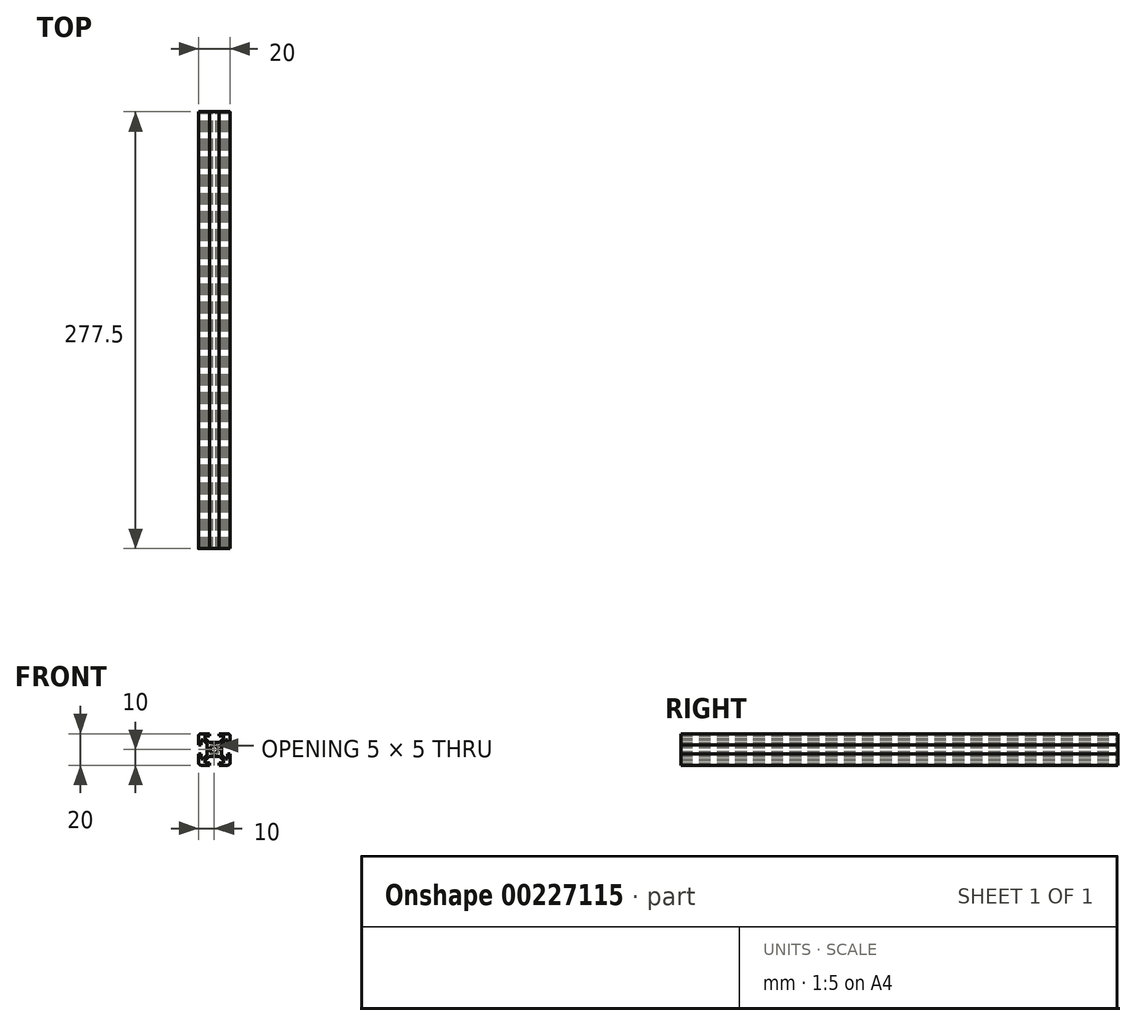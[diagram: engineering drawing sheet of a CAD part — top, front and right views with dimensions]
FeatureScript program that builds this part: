
annotation { "Feature Type Name" : "Feature", "Feature Type Description" : "" }
export const myFeature = defineFeature(function(context is Context, id is Id, definition is map)
    precondition{}
    {
        {
            var Q0;
            Q0=qCreatedBy(makeId("Front.planeOp"),FACE);
            var sketch = newSketch(context, id + "F0", { "sketchPlane" : qUnion([Q0])});
            skLineSegment(sketch, "E0.bottom", {"start": v(8.5, -10) * mm, "end": v(3, -10) * mm});
            skLineSegment(sketch, "E0.top", {"start": v(8.5, 10) * mm, "end": v(3, 10) * mm});
            skLineSegment(sketch, "E0.left", {"start": v(10, -8.5) * mm, "end": v(10, -3) * mm});
            skLineSegment(sketch, "E0.right", {"start": v(-10, -8.5) * mm, "end": v(-10, -3) * mm});
            skPoint(sketch, "E0.middle", {"position": v(0, 0) * mm});
            skLineSegment(sketch, "E1.bottom", {"start": v(6, -8.5) * mm, "end": v(3, -8.5) * mm});
            skLineSegment(sketch, "E1.top", {"start": v(6, 8.5) * mm, "end": v(3, 8.5) * mm});
            skLineSegment(sketch, "E1.left", {"start": v(8.5, -6) * mm, "end": v(8.5, -3) * mm});
            skLineSegment(sketch, "E1.right", {"start": v(-8.5, -6) * mm, "end": v(-8.5, -3) * mm});
            skLineSegment(sketch, "E2.bottom", {"start": v(3.44, -4.5) * mm, "end": v(-3.44, -4.5) * mm});
            skLineSegment(sketch, "E2.top", {"start": v(3.44, 4.5) * mm, "end": v(-3.44, 4.5) * mm});
            skLineSegment(sketch, "E2.left", {"start": v(4.5, -3.44) * mm, "end": v(4.5, 3.44) * mm});
            skLineSegment(sketch, "E2.right", {"start": v(-4.5, -3.44) * mm, "end": v(-4.5, 3.44) * mm});
            skLineSegment(sketch, "E3.bottom", {"start": v(8.5, -6) * mm, "end": v(7.06, -6) * mm});
            skLineSegment(sketch, "E3.top", {"start": v(8.5, 6) * mm, "end": v(7.06, 6) * mm});
            skLineSegment(sketch, "E4.left", {"start": v(6, -8.5) * mm, "end": v(6, -7.06) * mm});
            skLineSegment(sketch, "E4.right", {"start": v(-6, -8.5) * mm, "end": v(-6, -7.06) * mm});
            skPoint(sketch, "E5.orphan", {"position": v(-8.5, 8.5) * mm});
            skPoint(sketch, "E6.orphan", {"position": v(8.5, 8.5) * mm});
            skPoint(sketch, "E7.orphan", {"position": v(8.5, -8.5) * mm});
            skPoint(sketch, "E8.orphan", {"position": v(-8.5, -8.5) * mm});
            skLineSegment(sketch, "E9.trimOffspring", {"start": v(-6, 7.06) * mm, "end": v(-6, 8.5) * mm});
            skLineSegment(sketch, "E10.trimOffspring", {"start": v(-7.06, 6) * mm, "end": v(-8.5, 6) * mm});
            skLineSegment(sketch, "E11.trimOffspring", {"start": v(6, 7.06) * mm, "end": v(6, 8.5) * mm});
            skLineSegment(sketch, "E12.trimOffspring", {"start": v(-7.06, -6) * mm, "end": v(-8.5, -6) * mm});
            skLineSegment(sketch, "E13", {"start": v(-10, 10) * mm, "end": v(0, 0) * mm, "construction": true});
            skLineSegment(sketch, "E14", {"start": v(10, 10) * mm, "end": v(0, 0) * mm, "construction": true});
            skLineSegment(sketch, "E15", {"start": v(-6, 7.06) * mm, "end": v(-3.44, 4.5) * mm});
            skPoint(sketch, "E15.endSnap0", {"position": v(7.25, -6) * mm});
            skLineSegment(sketch, "E16", {"start": v(6, -7.06) * mm, "end": v(3.44, -4.5) * mm});
            skLineSegment(sketch, "E17", {"start": v(7.06, 6) * mm, "end": v(4.5, 3.44) * mm});
            skLineSegment(sketch, "E18", {"start": v(6, 7.06) * mm, "end": v(3.44, 4.5) * mm});
            skPoint(sketch, "E19.orphan", {"position": v(6, -6) * mm});
            skPoint(sketch, "E20.orphan", {"position": v(-4.5, -4.5) * mm});
            skPoint(sketch, "E21.orphan", {"position": v(-4.5, 4.5) * mm});
            skPoint(sketch, "E22.orphan", {"position": v(4.5, 4.5) * mm});
            skPoint(sketch, "E23.orphan", {"position": v(4.5, -4.5) * mm});
            skLineSegment(sketch, "E24.trimOffspring", {"start": v(4.5, -3.44) * mm, "end": v(7.06, -6) * mm});
            skLineSegment(sketch, "E25.trimOffspring", {"start": v(-3.44, -4.5) * mm, "end": v(-6, -7.06) * mm});
            skLineSegment(sketch, "E26.trimOffspring", {"start": v(-4.5, -3.44) * mm, "end": v(-7.06, -6) * mm});
            skLineSegment(sketch, "E27.trimOffspring", {"start": v(-4.5, 3.44) * mm, "end": v(-7.06, 6) * mm});
            skLineSegment(sketch, "E28.bottom", {"start": v(8.5, -3) * mm, "end": v(10, -3) * mm});
            skLineSegment(sketch, "E28.top", {"start": v(8.5, 3) * mm, "end": v(10, 3) * mm});
            skPoint(sketch, "E28.middle", {"position": v(10, 0) * mm});
            skLineSegment(sketch, "E29.left", {"start": v(3, 8.5) * mm, "end": v(3, 10) * mm});
            skLineSegment(sketch, "E29.right", {"start": v(-3, 8.5) * mm, "end": v(-3, 10) * mm});
            skPoint(sketch, "E29.middle", {"position": v(0, 10) * mm});
            skLineSegment(sketch, "E30.bottom", {"start": v(-8.5, 3) * mm, "end": v(-10, 3) * mm});
            skLineSegment(sketch, "E30.top", {"start": v(-8.5, -3) * mm, "end": v(-10, -3) * mm});
            skPoint(sketch, "E30.middle", {"position": v(-10, 0) * mm});
            skLineSegment(sketch, "E31.left", {"start": v(3, -8.5) * mm, "end": v(3, -10) * mm});
            skLineSegment(sketch, "E31.right", {"start": v(-3, -8.5) * mm, "end": v(-3, -10) * mm});
            skPoint(sketch, "E31.middle", {"position": v(0, -10) * mm});
            skPoint(sketch, "E32.orphan", {"position": v(3, 11.5) * mm});
            skPoint(sketch, "E33.orphan", {"position": v(-3, 11.5) * mm});
            skLineSegment(sketch, "E34.trimOffspring", {"start": v(-3, 10) * mm, "end": v(-8.5, 10) * mm});
            skLineSegment(sketch, "E35.trimOffspring", {"start": v(-3, 8.5) * mm, "end": v(-6, 8.5) * mm});
            skPoint(sketch, "E28.right.end.orphan", {"position": v(11.5, 3) * mm});
            skPoint(sketch, "E36.orphan", {"position": v(11.5, -3) * mm});
            skLineSegment(sketch, "E37.trimOffspring", {"start": v(10, 3) * mm, "end": v(10, 8.5) * mm});
            skLineSegment(sketch, "E38.trimOffspring", {"start": v(8.5, 3) * mm, "end": v(8.5, 6) * mm});
            skPoint(sketch, "E39.orphan", {"position": v(3, -11.5) * mm});
            skPoint(sketch, "E40.orphan", {"position": v(-3, -11.5) * mm});
            skLineSegment(sketch, "E41.trimOffspring", {"start": v(-3, -10) * mm, "end": v(-8.5, -10) * mm});
            skLineSegment(sketch, "E42.trimOffspring", {"start": v(-3, -8.5) * mm, "end": v(-6, -8.5) * mm});
            skPoint(sketch, "E30.right.end.orphan", {"position": v(-11.5, -3) * mm});
            skPoint(sketch, "E43.orphan", {"position": v(-11.5, 3) * mm});
            skLineSegment(sketch, "E44.trimOffspring", {"start": v(-10, 3) * mm, "end": v(-10, 8.5) * mm});
            skLineSegment(sketch, "E45.trimOffspring", {"start": v(-8.5, 3) * mm, "end": v(-8.5, 6) * mm});
            skLineSegment(sketch, "E46.trimOffspring", {"start": v(0, 0) * mm, "end": v(10, -10) * mm, "construction": true});
            skLineSegment(sketch, "E47.trimOffspring", {"start": v(0, 0) * mm, "end": v(-10, -10) * mm, "construction": true});
            skArc(sketch, "E48", {"start": v(1.16, 2.22) * mm, "mid": v(0, 2.5) * mm, "end": v(-1.16, 2.22) * mm});
            skLineSegment(sketch, "E49", {"start": v(-2.5, -1.44) * mm, "end": v(1.44, 2.5) * mm});
            skLineSegment(sketch, "E50", {"start": v(2.5, 1.44) * mm, "end": v(-1.44, -2.5) * mm});
            skLineSegment(sketch, "E51", {"start": v(1.44, -2.5) * mm, "end": v(-2.5, 1.44) * mm});
            skLineSegment(sketch, "E52", {"start": v(-1.44, 2.5) * mm, "end": v(2.5, -1.44) * mm});
            skLineSegment(sketch, "E53", {"start": v(2.5, 1.44) * mm, "end": v(2.5, -1.44) * mm, "construction": true});
            skLineSegment(sketch, "E54", {"start": v(1.44, -2.5) * mm, "end": v(-1.44, -2.5) * mm, "construction": true});
            skLineSegment(sketch, "E55", {"start": v(-2.5, -1.44) * mm, "end": v(-2.5, 1.44) * mm, "construction": true});
            skLineSegment(sketch, "E56", {"start": v(-1.44, 2.5) * mm, "end": v(1.44, 2.5) * mm, "construction": true});
            skLineSegment(sketch, "E57", {"start": v(-1.44, 2.5) * mm, "end": v(-2.5, 1.44) * mm});
            skLineSegment(sketch, "E58", {"start": v(1.44, 2.5) * mm, "end": v(2.5, 1.44) * mm});
            skLineSegment(sketch, "E59", {"start": v(2.5, -1.44) * mm, "end": v(1.44, -2.5) * mm});
            skLineSegment(sketch, "E60", {"start": v(-1.44, -2.5) * mm, "end": v(-2.5, -1.44) * mm});
            skArc(sketch, "E61.trimOffspring", {"start": v(-2.22, 1.16) * mm, "mid": v(-2.5, 0) * mm, "end": v(-2.22, -1.16) * mm});
            skArc(sketch, "E62.trimOffspring", {"start": v(-1.16, -2.22) * mm, "mid": v(0, -2.5) * mm, "end": v(1.16, -2.22) * mm});
            skArc(sketch, "E63.trimOffspring", {"start": v(2.22, -1.16) * mm, "mid": v(2.5, 0) * mm, "end": v(2.22, 1.16) * mm});
            skPoint(sketch, "E64.visualSharp", {"position": v(10, 10) * mm});
            skArc(sketch, "E64.filletArc", {"start": v(10, 8.5) * mm, "mid": v(9.56, 9.56) * mm, "end": v(8.5, 10) * mm});
            skPoint(sketch, "E65.visualSharp", {"position": v(10, -10) * mm});
            skArc(sketch, "E65.filletArc", {"start": v(8.5, -10) * mm, "mid": v(9.56, -9.56) * mm, "end": v(10, -8.5) * mm});
            skPoint(sketch, "E66.visualSharp", {"position": v(-10, -10) * mm});
            skArc(sketch, "E66.filletArc", {"start": v(-10, -8.5) * mm, "mid": v(-9.56, -9.56) * mm, "end": v(-8.5, -10) * mm});
            skPoint(sketch, "E67.visualSharp", {"position": v(-10, 10) * mm});
            skArc(sketch, "E67.filletArc", {"start": v(-8.5, 10) * mm, "mid": v(-9.56, 9.56) * mm, "end": v(-10, 8.5) * mm});
            skSolve(sketch);
        }
        {
            assignVariable(context, id + "F2", {"name" : "Length", "anyValue" : 277.5});
        }
        {
            var Q0;
            Q0=qSketchRegion(id+"F0",true);
            extrude(context, id + "F1", {"entities" : qUnion([Q0]), "depth" : (getVariable(context, 'Length')) * mm});
        }
    });
